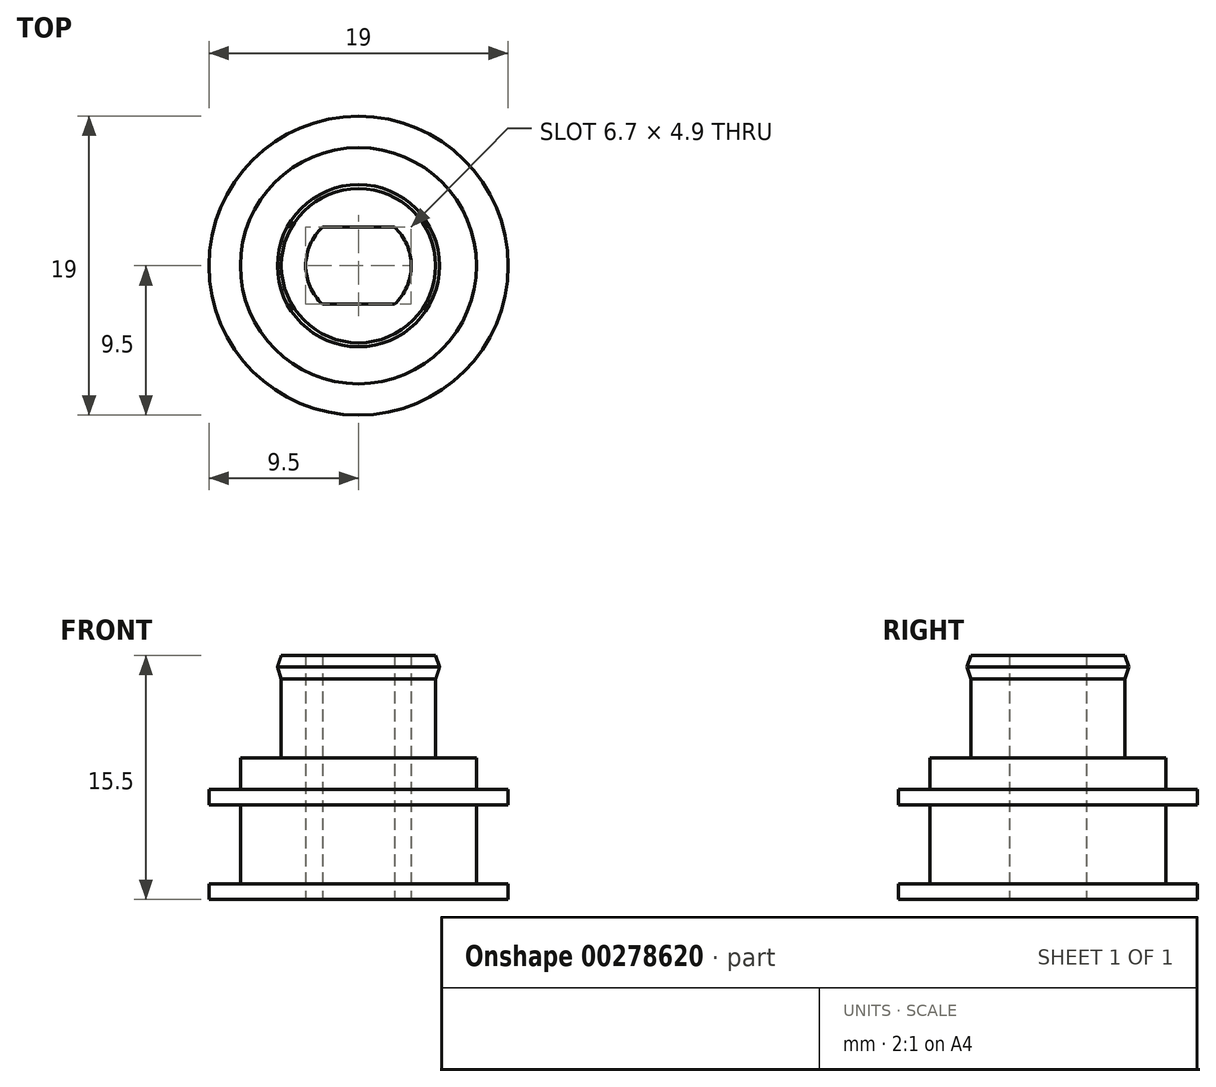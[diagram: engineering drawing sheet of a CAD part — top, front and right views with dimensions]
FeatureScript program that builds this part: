
annotation { "Feature Type Name" : "Feature", "Feature Type Description" : "" }
export const myFeature = defineFeature(function(context is Context, id is Id, definition is map)
    precondition{}
    {
        {
            assignVariable(context, id + "F0", {"name" : "e", "anyValue" : 3});
        }
        {
            assignVariable(context, id + "F1", {"name" : "h1", "anyValue" : 6});
        }
        {
            assignVariable(context, id + "F2", {"name" : "h2", "anyValue" : 6.5});
        }
        {
            var Q0;
            Q0=qCreatedBy(makeId("Top.planeOp"),FACE);
            var sketch = newSketch(context, id + "F3", { "sketchPlane" : qUnion([Q0])});
            skCircle(sketch, "E0", {"center": v(0, 0) * mm, "radius": 7.5 * mm});
            skCircle(sketch, "E1", {"center": v(0, 0) * mm, "radius": 4.9 * mm});
            skArc(sketch, "E2", {"start": v(-2.28, 2.45) * mm, "mid": v(-3.35, 0) * mm, "end": v(-2.28, -2.45) * mm});
            skLineSegment(sketch, "E3.bottom", {"start": v(2.28, -2.45) * mm, "end": v(-2.28, -2.45) * mm});
            skLineSegment(sketch, "E3.top", {"start": v(2.28, 2.45) * mm, "end": v(-2.28, 2.45) * mm});
            skArc(sketch, "E4.trimOffspring", {"start": v(2.28, -2.45) * mm, "mid": v(3.35, 0) * mm, "end": v(2.28, 2.45) * mm});
            skPoint(sketch, "E5.orphan", {"position": v(3.35, 2.45) * mm});
            skPoint(sketch, "E6.orphan", {"position": v(3.35, -2.45) * mm});
            skPoint(sketch, "E7.orphan", {"position": v(-3.35, -2.45) * mm});
            skPoint(sketch, "E8.orphan", {"position": v(-3.35, 2.45) * mm});
            skCircle(sketch, "E9", {"center": v(0, 0) * mm, "radius": 9.5 * mm});
            skSolve(sketch);
        }
        {
            var Q0;
            Q0=makeQuery(id+"F3.imprint","IMPRINT",FACE,{"disambiguationData":[TD([[makeQuery(id+"F3.imprint","IMPRINT",EDGE,{"derivedFrom":sQuery(id+"F3.wireOp",EDGE,"E9")}),1.0]])]});
            var Q1;
            Q1=makeQuery(id+"F3.imprint","IMPRINT",FACE,{"disambiguationData":[TD([[makeQuery(id+"F3.imprint","IMPRINT",EDGE,{"derivedFrom":sQuery(id+"F3.wireOp",EDGE,"E0")}),-1.0]])]});
            var Q2;
            Q2=makeQuery(id+"F3.imprint","IMPRINT",FACE,{"disambiguationData":[TD([[makeQuery(id+"F3.imprint","IMPRINT",EDGE,{"derivedFrom":sQuery(id+"F3.wireOp",EDGE,"E0")}),1.0]])]});
            var Q3;
            Q3=makeQuery(id+"F3.imprint","IMPRINT",FACE,{"disambiguationData":[TD([[makeQuery(id+"F3.imprint","IMPRINT",EDGE,{"derivedFrom":sQuery(id+"F3.wireOp",EDGE,"E1")}),1.0]])]});
            extrude(context, id + "F4", {"entities" : qUnion([Q0, Q1, Q2, Q3]), "depth" : 1 * mm});
        }
        {
            var Q0;
            Q0=makeQuery(id+"F4.opExtrude","SWEPT_BODY",BODY,{"disambiguationData":[OSD([sQuery(id+"F3.wireOp",EDGE,"E9"),sQuery(id+"F3.wireOp",EDGE,"EIqunKHo-nNsy-NuN7-MCyh-zDvAt2EbuDEc"),sQuery(id+"F3.wireOp",EDGE,"wDOxUPXS-ZM6U-Q8Jq-wcH9-EKwYlBhU692d"),sQuery(id+"F3.wireOp",EDGE,"eb7e76fe-5503-4f90-a268-9aebf731f32b0.MirrorCS"),sQuery(id+"F3.wireOp",EDGE,"KeFLWRGC-2lTl-id6V-Nq3M-w2rfNKTJ84NE"),sQuery(id+"F3.wireOp",EDGE,"b117cb93-11e5-48b8-9008-3f88b5f9d245.trimOffspring"),sQuery(id+"F3.wireOp",EDGE,"ce234f76-c4db-484e-b82a-35bcf09fa61d.1.0"),sQuery(id+"F3.wireOp",EDGE,"ce234f76-c4db-484e-b82a-35bcf09fa61d.1.1"),sQuery(id+"F3.wireOp",EDGE,"ce234f76-c4db-484e-b82a-35bcf09fa61d.1.2"),sQuery(id+"F3.wireOp",EDGE,"ce234f76-c4db-484e-b82a-35bcf09fa61d.1.3"),sQuery(id+"F3.wireOp",EDGE,"ce234f76-c4db-484e-b82a-35bcf09fa61d.1.4"),sQuery(id+"F3.wireOp",EDGE,"ce234f76-c4db-484e-b82a-35bcf09fa61d.2.0"),sQuery(id+"F3.wireOp",EDGE,"ce234f76-c4db-484e-b82a-35bcf09fa61d.2.1"),sQuery(id+"F3.wireOp",EDGE,"ce234f76-c4db-484e-b82a-35bcf09fa61d.2.2"),sQuery(id+"F3.wireOp",EDGE,"ce234f76-c4db-484e-b82a-35bcf09fa61d.2.3"),sQuery(id+"F3.wireOp",EDGE,"ce234f76-c4db-484e-b82a-35bcf09fa61d.2.4"),sQuery(id+"F3.wireOp",EDGE,"ce234f76-c4db-484e-b82a-35bcf09fa61d.3.0"),sQuery(id+"F3.wireOp",EDGE,"ce234f76-c4db-484e-b82a-35bcf09fa61d.3.1"),sQuery(id+"F3.wireOp",EDGE,"ce234f76-c4db-484e-b82a-35bcf09fa61d.3.2"),sQuery(id+"F3.wireOp",EDGE,"ce234f76-c4db-484e-b82a-35bcf09fa61d.3.3"),sQuery(id+"F3.wireOp",EDGE,"ce234f76-c4db-484e-b82a-35bcf09fa61d.3.4"),sQuery(id+"F3.wireOp",EDGE,"ce234f76-c4db-484e-b82a-35bcf09fa61d.4.0"),sQuery(id+"F3.wireOp",EDGE,"ce234f76-c4db-484e-b82a-35bcf09fa61d.4.1"),sQuery(id+"F3.wireOp",EDGE,"ce234f76-c4db-484e-b82a-35bcf09fa61d.4.2"),sQuery(id+"F3.wireOp",EDGE,"ce234f76-c4db-484e-b82a-35bcf09fa61d.4.3"),sQuery(id+"F3.wireOp",EDGE,"ce234f76-c4db-484e-b82a-35bcf09fa61d.4.4"),sQuery(id+"F3.wireOp",EDGE,"ce234f76-c4db-484e-b82a-35bcf09fa61d.5.0"),sQuery(id+"F3.wireOp",EDGE,"ce234f76-c4db-484e-b82a-35bcf09fa61d.5.1"),sQuery(id+"F3.wireOp",EDGE,"ce234f76-c4db-484e-b82a-35bcf09fa61d.5.2"),sQuery(id+"F3.wireOp",EDGE,"ce234f76-c4db-484e-b82a-35bcf09fa61d.5.3"),sQuery(id+"F3.wireOp",EDGE,"ce234f76-c4db-484e-b82a-35bcf09fa61d.5.4"),sQuery(id+"F3.wireOp",EDGE,"ce234f76-c4db-484e-b82a-35bcf09fa61d.6.0"),sQuery(id+"F3.wireOp",EDGE,"ce234f76-c4db-484e-b82a-35bcf09fa61d.6.1"),sQuery(id+"F3.wireOp",EDGE,"ce234f76-c4db-484e-b82a-35bcf09fa61d.6.2"),sQuery(id+"F3.wireOp",EDGE,"ce234f76-c4db-484e-b82a-35bcf09fa61d.6.3"),sQuery(id+"F3.wireOp",EDGE,"ce234f76-c4db-484e-b82a-35bcf09fa61d.6.4"),sQuery(id+"F3.wireOp",EDGE,"ce234f76-c4db-484e-b82a-35bcf09fa61d.7.0"),sQuery(id+"F3.wireOp",EDGE,"ce234f76-c4db-484e-b82a-35bcf09fa61d.7.1"),sQuery(id+"F3.wireOp",EDGE,"ce234f76-c4db-484e-b82a-35bcf09fa61d.7.2"),sQuery(id+"F3.wireOp",EDGE,"ce234f76-c4db-484e-b82a-35bcf09fa61d.7.3"),sQuery(id+"F3.wireOp",EDGE,"ce234f76-c4db-484e-b82a-35bcf09fa61d.7.4"),sQuery(id+"F3.wireOp",EDGE,"ce234f76-c4db-484e-b82a-35bcf09fa61d.8.0"),sQuery(id+"F3.wireOp",EDGE,"ce234f76-c4db-484e-b82a-35bcf09fa61d.8.1"),sQuery(id+"F3.wireOp",EDGE,"ce234f76-c4db-484e-b82a-35bcf09fa61d.8.2"),sQuery(id+"F3.wireOp",EDGE,"ce234f76-c4db-484e-b82a-35bcf09fa61d.8.3"),sQuery(id+"F3.wireOp",EDGE,"ce234f76-c4db-484e-b82a-35bcf09fa61d.8.4"),sQuery(id+"F3.wireOp",EDGE,"ce234f76-c4db-484e-b82a-35bcf09fa61d.9.0"),sQuery(id+"F3.wireOp",EDGE,"ce234f76-c4db-484e-b82a-35bcf09fa61d.9.1"),sQuery(id+"F3.wireOp",EDGE,"ce234f76-c4db-484e-b82a-35bcf09fa61d.9.2"),sQuery(id+"F3.wireOp",EDGE,"ce234f76-c4db-484e-b82a-35bcf09fa61d.9.3"),sQuery(id+"F3.wireOp",EDGE,"ce234f76-c4db-484e-b82a-35bcf09fa61d.9.4"),sQuery(id+"F3.wireOp",EDGE,"ce234f76-c4db-484e-b82a-35bcf09fa61d.10.0"),sQuery(id+"F3.wireOp",EDGE,"ce234f76-c4db-484e-b82a-35bcf09fa61d.10.1"),sQuery(id+"F3.wireOp",EDGE,"ce234f76-c4db-484e-b82a-35bcf09fa61d.10.2"),sQuery(id+"F3.wireOp",EDGE,"ce234f76-c4db-484e-b82a-35bcf09fa61d.10.3"),sQuery(id+"F3.wireOp",EDGE,"ce234f76-c4db-484e-b82a-35bcf09fa61d.10.4"),sQuery(id+"F3.wireOp",EDGE,"ce234f76-c4db-484e-b82a-35bcf09fa61d.11.0"),sQuery(id+"F3.wireOp",EDGE,"ce234f76-c4db-484e-b82a-35bcf09fa61d.11.1"),sQuery(id+"F3.wireOp",EDGE,"ce234f76-c4db-484e-b82a-35bcf09fa61d.11.2"),sQuery(id+"F3.wireOp",EDGE,"ce234f76-c4db-484e-b82a-35bcf09fa61d.11.3"),sQuery(id+"F3.wireOp",EDGE,"ce234f76-c4db-484e-b82a-35bcf09fa61d.11.4"),sQuery(id+"F3.wireOp",EDGE,"ce234f76-c4db-484e-b82a-35bcf09fa61d.12.0"),sQuery(id+"F3.wireOp",EDGE,"ce234f76-c4db-484e-b82a-35bcf09fa61d.12.1"),sQuery(id+"F3.wireOp",EDGE,"ce234f76-c4db-484e-b82a-35bcf09fa61d.12.2"),sQuery(id+"F3.wireOp",EDGE,"ce234f76-c4db-484e-b82a-35bcf09fa61d.12.3"),sQuery(id+"F3.wireOp",EDGE,"ce234f76-c4db-484e-b82a-35bcf09fa61d.12.4"),sQuery(id+"F3.wireOp",EDGE,"ce234f76-c4db-484e-b82a-35bcf09fa61d.13.0"),sQuery(id+"F3.wireOp",EDGE,"ce234f76-c4db-484e-b82a-35bcf09fa61d.13.1"),sQuery(id+"F3.wireOp",EDGE,"ce234f76-c4db-484e-b82a-35bcf09fa61d.13.2"),sQuery(id+"F3.wireOp",EDGE,"ce234f76-c4db-484e-b82a-35bcf09fa61d.13.3"),sQuery(id+"F3.wireOp",EDGE,"ce234f76-c4db-484e-b82a-35bcf09fa61d.13.4"),sQuery(id+"F3.wireOp",EDGE,"ce234f76-c4db-484e-b82a-35bcf09fa61d.14.0"),sQuery(id+"F3.wireOp",EDGE,"ce234f76-c4db-484e-b82a-35bcf09fa61d.14.1"),sQuery(id+"F3.wireOp",EDGE,"ce234f76-c4db-484e-b82a-35bcf09fa61d.14.2"),sQuery(id+"F3.wireOp",EDGE,"ce234f76-c4db-484e-b82a-35bcf09fa61d.14.3"),sQuery(id+"F3.wireOp",EDGE,"ce234f76-c4db-484e-b82a-35bcf09fa61d.14.4"),sQuery(id+"F3.wireOp",EDGE,"ce234f76-c4db-484e-b82a-35bcf09fa61d.15.0"),sQuery(id+"F3.wireOp",EDGE,"ce234f76-c4db-484e-b82a-35bcf09fa61d.15.1"),sQuery(id+"F3.wireOp",EDGE,"ce234f76-c4db-484e-b82a-35bcf09fa61d.15.2"),sQuery(id+"F3.wireOp",EDGE,"ce234f76-c4db-484e-b82a-35bcf09fa61d.15.3"),sQuery(id+"F3.wireOp",EDGE,"ce234f76-c4db-484e-b82a-35bcf09fa61d.15.4"),sQuery(id+"F3.wireOp",EDGE,"ce234f76-c4db-484e-b82a-35bcf09fa61d.16.0"),sQuery(id+"F3.wireOp",EDGE,"ce234f76-c4db-484e-b82a-35bcf09fa61d.16.1"),sQuery(id+"F3.wireOp",EDGE,"ce234f76-c4db-484e-b82a-35bcf09fa61d.16.2"),sQuery(id+"F3.wireOp",EDGE,"ce234f76-c4db-484e-b82a-35bcf09fa61d.16.3"),sQuery(id+"F3.wireOp",EDGE,"ce234f76-c4db-484e-b82a-35bcf09fa61d.16.4"),sQuery(id+"F3.wireOp",EDGE,"ce234f76-c4db-484e-b82a-35bcf09fa61d.17.0"),sQuery(id+"F3.wireOp",EDGE,"ce234f76-c4db-484e-b82a-35bcf09fa61d.17.1"),sQuery(id+"F3.wireOp",EDGE,"ce234f76-c4db-484e-b82a-35bcf09fa61d.17.2"),sQuery(id+"F3.wireOp",EDGE,"ce234f76-c4db-484e-b82a-35bcf09fa61d.17.3"),sQuery(id+"F3.wireOp",EDGE,"ce234f76-c4db-484e-b82a-35bcf09fa61d.17.4"),sQuery(id+"F3.wireOp",EDGE,"ce234f76-c4db-484e-b82a-35bcf09fa61d.18.0"),sQuery(id+"F3.wireOp",EDGE,"ce234f76-c4db-484e-b82a-35bcf09fa61d.18.1"),sQuery(id+"F3.wireOp",EDGE,"ce234f76-c4db-484e-b82a-35bcf09fa61d.18.2"),sQuery(id+"F3.wireOp",EDGE,"ce234f76-c4db-484e-b82a-35bcf09fa61d.18.3"),sQuery(id+"F3.wireOp",EDGE,"ce234f76-c4db-484e-b82a-35bcf09fa61d.18.4"),sQuery(id+"F3.wireOp",EDGE,"ce234f76-c4db-484e-b82a-35bcf09fa61d.19.0"),sQuery(id+"F3.wireOp",EDGE,"ce234f76-c4db-484e-b82a-35bcf09fa61d.19.1"),sQuery(id+"F3.wireOp",EDGE,"ce234f76-c4db-484e-b82a-35bcf09fa61d.19.2"),sQuery(id+"F3.wireOp",EDGE,"ce234f76-c4db-484e-b82a-35bcf09fa61d.19.3"),sQuery(id+"F3.wireOp",EDGE,"ce234f76-c4db-484e-b82a-35bcf09fa61d.19.4"),sQuery(id+"F3.wireOp",EDGE,"ce234f76-c4db-484e-b82a-35bcf09fa61d.20.0"),sQuery(id+"F3.wireOp",EDGE,"ce234f76-c4db-484e-b82a-35bcf09fa61d.20.1"),sQuery(id+"F3.wireOp",EDGE,"ce234f76-c4db-484e-b82a-35bcf09fa61d.20.2"),sQuery(id+"F3.wireOp",EDGE,"ce234f76-c4db-484e-b82a-35bcf09fa61d.20.3"),sQuery(id+"F3.wireOp",EDGE,"ce234f76-c4db-484e-b82a-35bcf09fa61d.20.4"),sQuery(id+"F3.wireOp",EDGE,"ce234f76-c4db-484e-b82a-35bcf09fa61d.21.0"),sQuery(id+"F3.wireOp",EDGE,"ce234f76-c4db-484e-b82a-35bcf09fa61d.21.1"),sQuery(id+"F3.wireOp",EDGE,"ce234f76-c4db-484e-b82a-35bcf09fa61d.21.2"),sQuery(id+"F3.wireOp",EDGE,"ce234f76-c4db-484e-b82a-35bcf09fa61d.21.3"),sQuery(id+"F3.wireOp",EDGE,"ce234f76-c4db-484e-b82a-35bcf09fa61d.21.4"),sQuery(id+"F3.wireOp",EDGE,"ce234f76-c4db-484e-b82a-35bcf09fa61d.22.0"),sQuery(id+"F3.wireOp",EDGE,"ce234f76-c4db-484e-b82a-35bcf09fa61d.22.1"),sQuery(id+"F3.wireOp",EDGE,"ce234f76-c4db-484e-b82a-35bcf09fa61d.22.2"),sQuery(id+"F3.wireOp",EDGE,"ce234f76-c4db-484e-b82a-35bcf09fa61d.22.3"),sQuery(id+"F3.wireOp",EDGE,"ce234f76-c4db-484e-b82a-35bcf09fa61d.22.4"),sQuery(id+"F3.wireOp",EDGE,"ce234f76-c4db-484e-b82a-35bcf09fa61d.23.0"),sQuery(id+"F3.wireOp",EDGE,"ce234f76-c4db-484e-b82a-35bcf09fa61d.23.1"),sQuery(id+"F3.wireOp",EDGE,"ce234f76-c4db-484e-b82a-35bcf09fa61d.23.2"),sQuery(id+"F3.wireOp",EDGE,"ce234f76-c4db-484e-b82a-35bcf09fa61d.23.3"),sQuery(id+"F3.wireOp",EDGE,"ce234f76-c4db-484e-b82a-35bcf09fa61d.23.4"),sQuery(id+"F3.wireOp",EDGE,"ce234f76-c4db-484e-b82a-35bcf09fa61d.24.0"),sQuery(id+"F3.wireOp",EDGE,"ce234f76-c4db-484e-b82a-35bcf09fa61d.24.1"),sQuery(id+"F3.wireOp",EDGE,"ce234f76-c4db-484e-b82a-35bcf09fa61d.24.2"),sQuery(id+"F3.wireOp",EDGE,"ce234f76-c4db-484e-b82a-35bcf09fa61d.24.3"),sQuery(id+"F3.wireOp",EDGE,"ce234f76-c4db-484e-b82a-35bcf09fa61d.24.4"),sQuery(id+"F3.wireOp",EDGE,"ce234f76-c4db-484e-b82a-35bcf09fa61d.25.0"),sQuery(id+"F3.wireOp",EDGE,"ce234f76-c4db-484e-b82a-35bcf09fa61d.25.1"),sQuery(id+"F3.wireOp",EDGE,"ce234f76-c4db-484e-b82a-35bcf09fa61d.25.2"),sQuery(id+"F3.wireOp",EDGE,"ce234f76-c4db-484e-b82a-35bcf09fa61d.25.3"),sQuery(id+"F3.wireOp",EDGE,"ce234f76-c4db-484e-b82a-35bcf09fa61d.25.4"),sQuery(id+"F3.wireOp",EDGE,"ce234f76-c4db-484e-b82a-35bcf09fa61d.26.0"),sQuery(id+"F3.wireOp",EDGE,"ce234f76-c4db-484e-b82a-35bcf09fa61d.26.1"),sQuery(id+"F3.wireOp",EDGE,"ce234f76-c4db-484e-b82a-35bcf09fa61d.26.2"),sQuery(id+"F3.wireOp",EDGE,"ce234f76-c4db-484e-b82a-35bcf09fa61d.26.3"),sQuery(id+"F3.wireOp",EDGE,"ce234f76-c4db-484e-b82a-35bcf09fa61d.26.4"),sQuery(id+"F3.wireOp",EDGE,"ce234f76-c4db-484e-b82a-35bcf09fa61d.27.0"),sQuery(id+"F3.wireOp",EDGE,"ce234f76-c4db-484e-b82a-35bcf09fa61d.27.1"),sQuery(id+"F3.wireOp",EDGE,"ce234f76-c4db-484e-b82a-35bcf09fa61d.27.2"),sQuery(id+"F3.wireOp",EDGE,"ce234f76-c4db-484e-b82a-35bcf09fa61d.27.3"),sQuery(id+"F3.wireOp",EDGE,"ce234f76-c4db-484e-b82a-35bcf09fa61d.27.4"),sQuery(id+"F3.wireOp",EDGE,"ce234f76-c4db-484e-b82a-35bcf09fa61d.28.0"),sQuery(id+"F3.wireOp",EDGE,"ce234f76-c4db-484e-b82a-35bcf09fa61d.28.1"),sQuery(id+"F3.wireOp",EDGE,"ce234f76-c4db-484e-b82a-35bcf09fa61d.28.2"),sQuery(id+"F3.wireOp",EDGE,"ce234f76-c4db-484e-b82a-35bcf09fa61d.28.3"),sQuery(id+"F3.wireOp",EDGE,"ce234f76-c4db-484e-b82a-35bcf09fa61d.28.4"),sQuery(id+"F3.wireOp",EDGE,"ce234f76-c4db-484e-b82a-35bcf09fa61d.29.0"),sQuery(id+"F3.wireOp",EDGE,"ce234f76-c4db-484e-b82a-35bcf09fa61d.29.1"),sQuery(id+"F3.wireOp",EDGE,"ce234f76-c4db-484e-b82a-35bcf09fa61d.29.2"),sQuery(id+"F3.wireOp",EDGE,"ce234f76-c4db-484e-b82a-35bcf09fa61d.29.3"),sQuery(id+"F3.wireOp",EDGE,"ce234f76-c4db-484e-b82a-35bcf09fa61d.29.4")])]});
            transform(context, id + "F5", {"entities" : qUnion([Q0]), "transformType" : TransformType.TRANSLATION_3D, "dx" : 0 * mm, "dy" : 0 * mm, "dz" : 6 * mm, "makeCopy" : true});
        }
        {
            var Q0;
            Q0=makeQuery(id+"F3.imprint","IMPRINT",FACE,{"disambiguationData":[TD([[makeQuery(id+"F3.imprint","IMPRINT",EDGE,{"derivedFrom":sQuery(id+"F3.wireOp",EDGE,"E0")}),1.0]])]});
            var Q1;
            Q1=makeQuery(id+"F3.imprint","IMPRINT",FACE,{"disambiguationData":[TD([[makeQuery(id+"F3.imprint","IMPRINT",EDGE,{"derivedFrom":sQuery(id+"F3.wireOp",EDGE,"E1")}),1.0]])]});
            extrude(context, id + "F6", {"entities" : qUnion([Q0, Q1]), "depth" : 9 * mm});
        }
        {
            var Q0;
            Q0=makeQuery(id+"F3.imprint","IMPRINT",FACE,{"disambiguationData":[TD([[makeQuery(id+"F3.imprint","IMPRINT",EDGE,{"derivedFrom":sQuery(id+"F3.wireOp",EDGE,"E1")}),1.0]])]});
            extrude(context, id + "F7", {"entities" : qUnion([Q0]), "operationType" : NewBodyOperationType.ADD, "depth" : (getVariable(context, 'e') + getVariable(context, 'h1') + getVariable(context, 'h2')) * mm});
        }
        {
            var Q0;
            Q0=qCreatedBy(makeId("Front.planeOp"),FACE);
            var sketch = newSketch(context, id + "F8", { "sketchPlane" : qUnion([Q0])});
            skLineSegment(sketch, "E10", {"start": v(0, 0) * mm, "end": v(0, 17.5) * mm, "construction": true});
            skLineSegment(sketch, "E11", {"start": v(-4.9, 6) * mm, "end": v(-4.9, 12.5) * mm});
            skLineSegment(sketch, "E12", {"start": v(4.9, 15.5) * mm, "end": v(4.9, 6) * mm});
            skLineSegment(sketch, "E13.bottom", {"start": v(4.9, 15.5) * mm, "end": v(5.15, 15.5) * mm, "construction": true});
            skLineSegment(sketch, "E13.top", {"start": v(4.9, 14) * mm, "end": v(5.15, 14) * mm, "construction": true});
            skLineSegment(sketch, "E13.left", {"start": v(4.9, 15.5) * mm, "end": v(4.9, 14) * mm, "construction": true});
            skLineSegment(sketch, "E13.right", {"start": v(5.15, 15.5) * mm, "end": v(5.15, 14) * mm, "construction": true});
            skPoint(sketch, "E14", {"position": v(5.15, 14.75) * mm});
            skLineSegment(sketch, "E15", {"start": v(4.9, 15.5) * mm, "end": v(5.15, 14.75) * mm});
            skLineSegment(sketch, "E16", {"start": v(5.15, 14.75) * mm, "end": v(4.9, 14) * mm});
            skLineSegment(sketch, "E17", {"start": v(4.9, 14) * mm, "end": v(4.9, 15.5) * mm});
            skSolve(sketch);
        }
        {
            var Q0;
            Q0=makeQuery(id+"F8.imprint","IMPRINT",FACE,{"disambiguationData":[TD([[makeQuery(id+"F8.imprint","IMPRINT",EDGE,{"derivedFrom":sQuery(id+"F8.wireOp",EDGE,"E15")}),-1.0]])]});
            var Q1;
            Q1=sQuery(id+"F8.wireOp",EDGE,"E10");
            revolve(context, id + "F9", {"operationType" : NewBodyOperationType.ADD, "entities" : qUnion([Q0]), "axis" : qUnion([Q1]), "revolveType" : RevolveType.FULL});
        }
        {
            var Q0;
            Q0=makeQuery(id+"F7.opExtrude","CAP_FACE",FACE,{"disambiguationData":[OSD([sQuery(id+"F3.wireOp",EDGE,"E1"),sQuery(id+"F3.wireOp",EDGE,"E2"),sQuery(id+"F3.wireOp",EDGE,"E3.bottom"),sQuery(id+"F3.wireOp",EDGE,"E3.top"),sQuery(id+"F3.wireOp",EDGE,"E4.trimOffspring")])],"isStart":false});
            cPlane(context, id + "F10", {"entities" : qUnion([Q0]), "cplaneType" : CPlaneType.OFFSET, "offset" : 0 * mm, "width" : 150 * mm, "height" : 150 * mm});
        }
        {
            var Q0;
            Q0=qCreatedBy(id+"F10.planeOp",FACE);
            var sketch = newSketch(context, id + "F11", { "sketchPlane" : qUnion([Q0])});
            skArc(sketch, "E18", {"start": v(-2.38, 2.7) * mm, "mid": v(-3.6, 0) * mm, "end": v(-2.38, -2.7) * mm});
            skLineSegment(sketch, "E19.bottom", {"start": v(-2.38, 2.7) * mm, "end": v(2.38, 2.7) * mm});
            skLineSegment(sketch, "E19.top", {"start": v(-2.38, -2.7) * mm, "end": v(2.38, -2.7) * mm});
            skPoint(sketch, "E20.orphan", {"position": v(4.18, 2.7) * mm});
            skPoint(sketch, "E21.orphan", {"position": v(3.52, -2.7) * mm});
            skArc(sketch, "E22.trimOffspring", {"start": v(2.38, -2.7) * mm, "mid": v(3.6, 0) * mm, "end": v(2.38, 2.7) * mm});
            skPoint(sketch, "E23.orphan", {"position": v(-4.18, -2.7) * mm});
            skPoint(sketch, "E24.orphan", {"position": v(-3.52, 2.7) * mm});
            skSolve(sketch);
        }
    });
